# Revit family: Поддон для  VKR
name_source: partatom
category: Оборудование
revit_build: Autodesk Revit 2017 (Build: 20170118_1100(x64)
units: mm (PartAtom-declared; Revit-internal decimal feet)

## family parameters
Всегда вертикально = Да
На основе рабочей плоскости = Нет
Общий = Нет
При загрузке вырезать с полостями = Нет
Размер круглого соединителя = Использовать диаметр
Тип детали = Нормальный
Точка расчета площади = Нет

## types (7) — shared parameters
ADSK_Единица измерения = шт.
ADSK_Завод-изготовитель = NEVATOM
Nevatom_URL = https://t.me
высота ободка = 30 мм
материал = Сталь оцинкованная
материал на выбор = Сталь нержавеющая
толщина изделия = 3 мм

## per-type parameters (varying)
| type | ADSK_Марка | ADSK_Наименование | a | b | k | высота | высота лепестка | длина | ширина |
| Поддон для SMK-040 | SMK-040 | Поддон для SMK-040 | 28 мм | 28 мм | 67 мм | 100 мм | 70 мм | 465 мм | 465 мм |
| Поддон для SMK-063 | SMK-063 | Поддон VKR.PDK.063.01.001 | 49 мм | 49 мм | 117 мм | 150 мм | 120 мм | 890 мм | 890 мм |
| Поддон для SMK-031 | SMK-031 | Поддон для SMK-031 | 28 мм | 28 мм | 67 мм | 100 мм | 70 мм | 465 мм | 465 мм |
| Поддон для SMK-050 | SMK-050 | Поддон для SMK-050 | 49 мм | 49 мм | 117 мм | 150 мм | 120 мм | 891 мм | 891 мм |
| Поддон для SMK-100 | SMK-100 | Поддон для SMK-100 | 50 мм | 50 мм | 167 мм | 200 мм | 170 мм | 1471 мм | 1471 мм |
| Поддон для SMK-125 | SMK-125 | Поддон для SMK-125 | 50 мм | 50 мм | 267 мм | 300 мм | 270 мм | 1471 мм | 1471 мм |
| Поддон для SMK-080 | SMK-080 | Поддон для SMK-080 | 49 мм | 49 мм | 117 мм | 150 мм | 120 мм | 967 мм | 967 мм |
